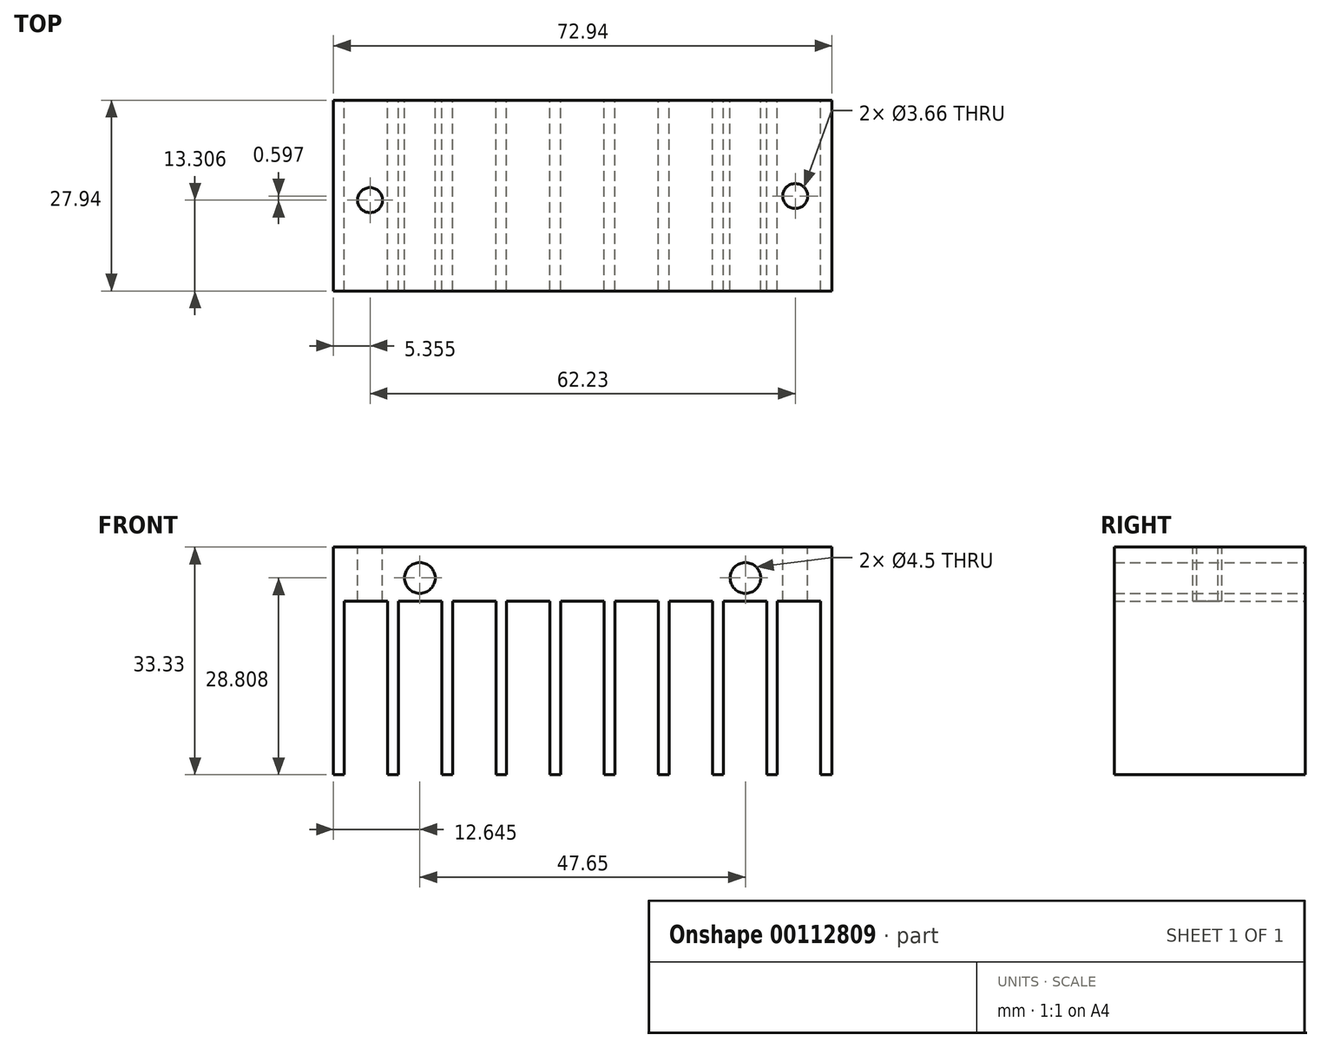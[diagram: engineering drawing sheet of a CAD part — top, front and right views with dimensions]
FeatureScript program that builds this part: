
annotation { "Feature Type Name" : "Feature", "Feature Type Description" : "" }
export const myFeature = defineFeature(function(context is Context, id is Id, definition is map)
    precondition{}
    {
        {
            var Q0;
            Q0=qCreatedBy(makeId("Front.planeOp"),FACE);
            var sketch = newSketch(context, id + "F0", { "sketchPlane" : qUnion([Q0])});
            skLineSegment(sketch, "E0.bottom", {"start": v(-36.47, -14.68) * mm, "end": v(-34.9, -14.68) * mm});
            skLineSegment(sketch, "E0.top", {"start": v(-36.47, 18.65) * mm, "end": v(36.47, 18.65) * mm});
            skLineSegment(sketch, "E0.left", {"start": v(-36.47, -14.68) * mm, "end": v(-36.47, 18.65) * mm});
            skLineSegment(sketch, "E0.right", {"start": v(36.47, -14.68) * mm, "end": v(36.47, 18.65) * mm});
            skLineSegment(sketch, "E1", {"start": v(-34.9, 10.72) * mm, "end": v(-28.55, 10.72) * mm});
            skCircle(sketch, "E2", {"center": v(-23.83, 14.13) * mm, "radius": 2.25 * mm});
            skCircle(sketch, "E3", {"center": v(23.83, 14.13) * mm, "radius": 2.25 * mm});
            skLineSegment(sketch, "E4", {"start": v(-34.9, 10.72) * mm, "end": v(-34.9, -14.68) * mm});
            skLineSegment(sketch, "E5", {"start": v(-28.55, 10.72) * mm, "end": v(-28.55, -14.68) * mm});
            skLineSegment(sketch, "E6", {"start": v(-26.97, 10.72) * mm, "end": v(-26.97, -14.68) * mm});
            skLineSegment(sketch, "E7", {"start": v(-20.62, 10.72) * mm, "end": v(-20.62, -14.68) * mm});
            skLineSegment(sketch, "E8", {"start": v(-19.05, 10.72) * mm, "end": v(-19.05, -14.68) * mm});
            skLineSegment(sketch, "E9.1.0.0", {"start": v(-11.13, 10.72) * mm, "end": v(-11.13, -14.68) * mm});
            skLineSegment(sketch, "E9.2.0.0", {"start": v(-3.2, 10.72) * mm, "end": v(-3.2, -14.68) * mm});
            skLineSegment(sketch, "E9.3.0.0", {"start": v(4.72, 10.72) * mm, "end": v(4.72, -14.68) * mm});
            skLineSegment(sketch, "E9.4.0.0", {"start": v(12.65, 10.72) * mm, "end": v(12.65, -14.68) * mm});
            skLineSegment(sketch, "E9.5.0.0", {"start": v(20.57, 10.72) * mm, "end": v(20.57, -14.68) * mm});
            skLineSegment(sketch, "E9.6.0.0", {"start": v(28.5, 10.72) * mm, "end": v(28.5, -14.68) * mm});
            skLineSegment(sketch, "E9.direction1", {"start": v(-12.7, -14.68) * mm, "end": v(-11.13, -14.68) * mm, "construction": true});
            skLineSegment(sketch, "E10.1.0.0", {"start": v(-12.7, 10.72) * mm, "end": v(-12.7, -14.68) * mm});
            skLineSegment(sketch, "E10.2.0.0", {"start": v(-4.78, 10.72) * mm, "end": v(-4.78, -14.68) * mm});
            skLineSegment(sketch, "E10.3.0.0", {"start": v(3.15, 10.72) * mm, "end": v(3.15, -14.68) * mm});
            skLineSegment(sketch, "E10.4.0.0", {"start": v(11.07, 10.72) * mm, "end": v(11.07, -14.68) * mm});
            skLineSegment(sketch, "E10.5.0.0", {"start": v(19, 10.72) * mm, "end": v(19, -14.68) * mm});
            skLineSegment(sketch, "E10.6.0.0", {"start": v(26.92, 10.72) * mm, "end": v(26.92, -14.68) * mm});
            skLineSegment(sketch, "E10.7.0.0", {"start": v(34.85, 10.72) * mm, "end": v(34.85, -14.68) * mm});
            skLineSegment(sketch, "E10.direction1", {"start": v(-20.62, -14.68) * mm, "end": v(-19.05, -14.68) * mm, "construction": true});
            skLineSegment(sketch, "E11.trimOffspring", {"start": v(-28.55, -14.68) * mm, "end": v(-26.97, -14.68) * mm});
            skLineSegment(sketch, "E12.trimOffspring", {"start": v(-20.62, -14.68) * mm, "end": v(-19.05, -14.68) * mm});
            skLineSegment(sketch, "E13.trimOffspring", {"start": v(-4.78, -14.68) * mm, "end": v(-3.2, -14.68) * mm});
            skLineSegment(sketch, "E14.trimOffspring", {"start": v(-12.7, -14.68) * mm, "end": v(-11.13, -14.68) * mm});
            skLineSegment(sketch, "E15.trimOffspring", {"start": v(3.15, -14.68) * mm, "end": v(4.72, -14.68) * mm});
            skLineSegment(sketch, "E16.trimOffspring", {"start": v(11.07, -14.68) * mm, "end": v(12.65, -14.68) * mm});
            skLineSegment(sketch, "E17.trimOffspring", {"start": v(19, -14.68) * mm, "end": v(20.57, -14.68) * mm});
            skLineSegment(sketch, "E18.trimOffspring", {"start": v(26.92, -14.68) * mm, "end": v(28.5, -14.68) * mm});
            skLineSegment(sketch, "E19.trimOffspring", {"start": v(34.85, -14.68) * mm, "end": v(36.47, -14.68) * mm});
            skLineSegment(sketch, "E20.trimOffspring", {"start": v(-26.97, 10.72) * mm, "end": v(-20.62, 10.72) * mm});
            skLineSegment(sketch, "E21.trimOffspring", {"start": v(-19.05, 10.72) * mm, "end": v(-12.7, 10.72) * mm});
            skLineSegment(sketch, "E22.trimOffspring", {"start": v(-11.13, 10.72) * mm, "end": v(-4.78, 10.72) * mm});
            skLineSegment(sketch, "E23.trimOffspring", {"start": v(-3.2, 10.72) * mm, "end": v(3.15, 10.72) * mm});
            skLineSegment(sketch, "E24.trimOffspring", {"start": v(4.72, 10.72) * mm, "end": v(11.07, 10.72) * mm});
            skLineSegment(sketch, "E25.trimOffspring", {"start": v(12.65, 10.72) * mm, "end": v(19, 10.72) * mm});
            skLineSegment(sketch, "E26.trimOffspring", {"start": v(20.57, 10.72) * mm, "end": v(26.92, 10.72) * mm});
            skLineSegment(sketch, "E27.trimOffspring", {"start": v(28.5, 10.72) * mm, "end": v(34.85, 10.72) * mm});
            skSolve(sketch);
        }
        {
            var Q0;
            Q0=makeQuery(id+"F0.imprint","IMPRINT",FACE,{"disambiguationData":[TD([[makeQuery(id+"F0.imprint","IMPRINT",EDGE,{"derivedFrom":sQuery(id+"F0.wireOp",EDGE,"E0.bottom")}),1.0]])]});
            extrude(context, id + "F1", {"entities" : qUnion([Q0]), "depth" : 27.94 * mm});
        }
        {
            var Q0;
            Q0=makeQuery(id+"F1.opExtrude","SWEPT_FACE",FACE,{"disambiguationData":[OSD([sQuery(id+"F0.wireOp",EDGE,"E0.top")])]});
            var sketch = newSketch(context, id + "F2", { "sketchPlane" : qUnion([Q0])});
            skPoint(sketch, "E28.endSnap0", {"position": v(36.47, -13.97) * mm});
            skCircle(sketch, "E29", {"center": v(31.12, -14.04) * mm, "radius": 1.83 * mm});
            skCircle(sketch, "E30", {"center": v(-31.12, -14.63) * mm, "radius": 1.83 * mm});
            skPoint(sketch, "E31.end.orphan", {"position": v(31.12, -31.1) * mm});
            skPoint(sketch, "E32.orphan", {"position": v(38.07, -13.97) * mm});
            skPoint(sketch, "E33.orphan", {"position": v(-31.12, -31.1) * mm});
            skSolve(sketch);
        }
        {
            var Q0;
            Q0=makeQuery(id+"F2.imprint","IMPRINT",FACE,{"disambiguationData":[TD([[makeQuery(id+"F2.imprint","IMPRINT",EDGE,{"derivedFrom":sQuery(id+"F2.wireOp",EDGE,"E30")}),1.0]])]});
            extrude(context, id + "F3", {"entities" : qUnion([Q0]), "operationType" : NewBodyOperationType.REMOVE, "endBound" : BoundingType.THROUGH_ALL, "oppositeDirection" : true, "depth" : 25.4 * mm});
        }
        {
            var Q0;
            Q0 = qSketchRegion(id + "F2", true);
            extrude(context, id + "F4", {"entities" : qUnion([Q0]), "operationType" : NewBodyOperationType.REMOVE, "endBound" : BoundingType.THROUGH_ALL, "oppositeDirection" : true, "depth" : 25.4 * mm});
        }
    });
